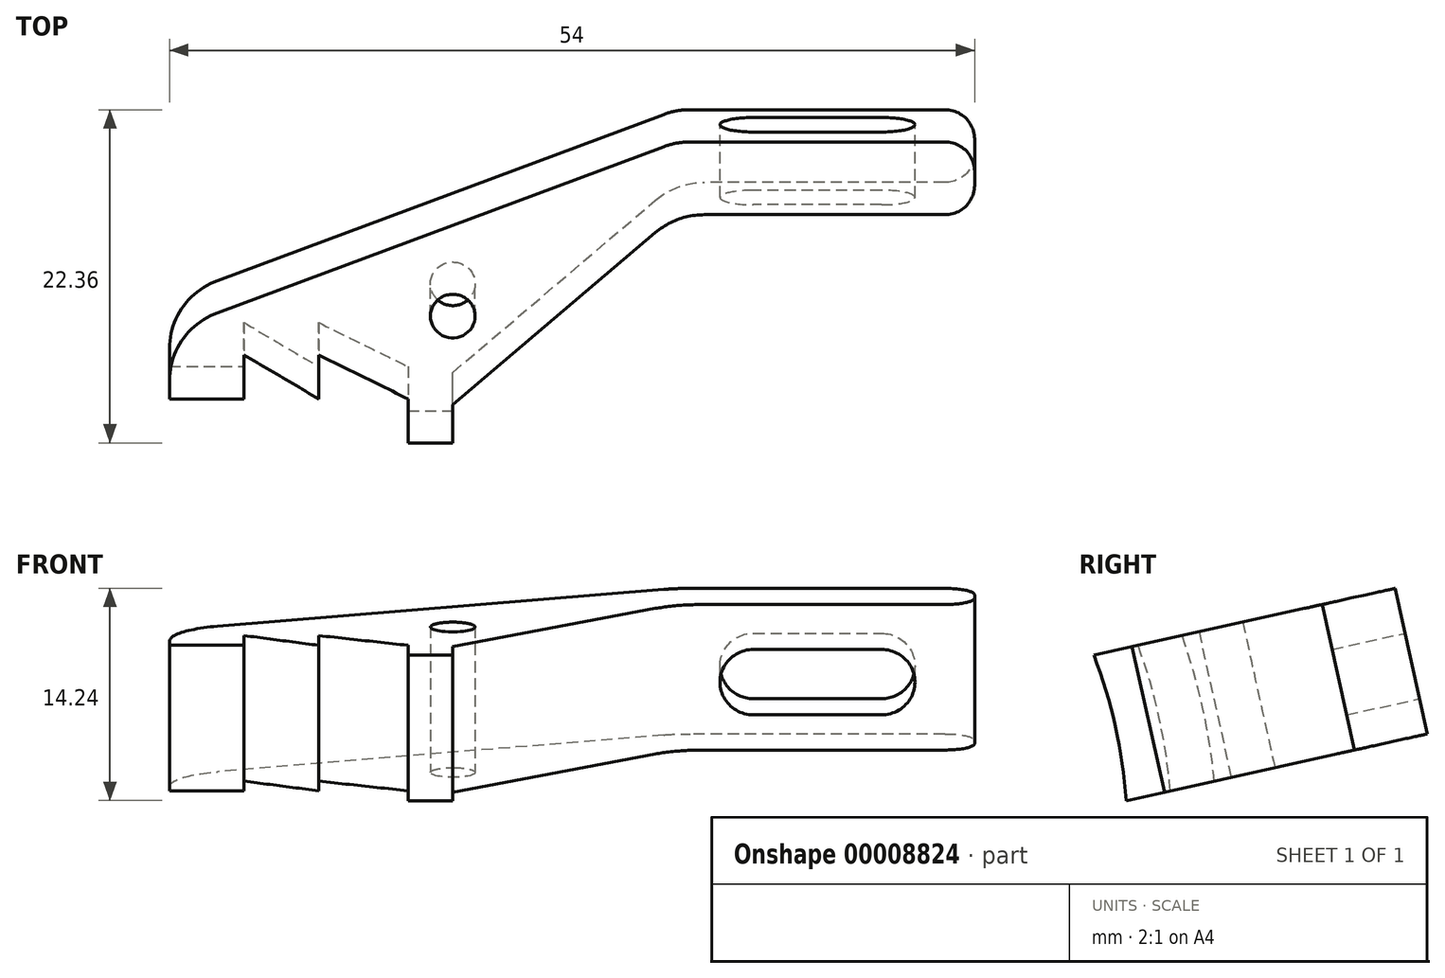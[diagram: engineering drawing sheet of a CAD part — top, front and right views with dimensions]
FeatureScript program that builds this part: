
annotation { "Feature Type Name" : "Feature", "Feature Type Description" : "" }
export const myFeature = defineFeature(function(context is Context, id is Id, definition is map)
    precondition{}
    {
        {
            var Q0;
            Q0=qCreatedBy(makeId("Top.planeOp"),FACE);
            var sketch = newSketch(context, id + "F0", { "sketchPlane" : qUnion([Q0])});
            skLineSegment(sketch, "E0", {"start": v(0, 0) * mm, "end": v(5, 0) * mm});
            skLineSegment(sketch, "E1", {"start": v(5, 0) * mm, "end": v(5, 3) * mm});
            skLineSegment(sketch, "E2", {"start": v(5, 3) * mm, "end": v(10, 0) * mm});
            skLineSegment(sketch, "E3", {"start": v(10, 0) * mm, "end": v(10, 3) * mm});
            skLineSegment(sketch, "E4", {"start": v(10, 3) * mm, "end": v(16, 0) * mm});
            skLineSegment(sketch, "E5", {"start": v(16, 0) * mm, "end": v(16, -3) * mm});
            skLineSegment(sketch, "E6", {"start": v(16, -3) * mm, "end": v(19, -3) * mm});
            skLineSegment(sketch, "E7", {"start": v(19, -3) * mm, "end": v(19, 5) * mm});
            skLineSegment(sketch, "E8", {"start": v(19, 5) * mm, "end": v(0, 5) * mm});
            skLineSegment(sketch, "E9", {"start": v(0, 5) * mm, "end": v(0, 0) * mm});
            skSolve(sketch);
        }
        {
            var Q0;
            Q0=qCreatedBy(makeId("Right.planeOp"),FACE);
            var sketch = newSketch(context, id + "F1", { "sketchPlane" : qUnion([Q0])});
            skArc(sketch, "E10", {"start": v(3, 0) * mm, "mid": v(2.05, 8.66) * mm, "end": v(-0.75, 16.9) * mm});
            skLineSegment(sketch, "E11", {"start": v(3, 0) * mm, "end": v(-37, 0) * mm});
            skLineSegment(sketch, "E12", {"start": v(-37, 0) * mm, "end": v(-0.75, 16.9) * mm});
            skSolve(sketch);
        }
        {
            var Q0;
            Q0=makeQuery(id+"F0.imprint","IMPRINT",FACE,{"disambiguationData":[TD([[makeQuery(id+"F0.imprint","IMPRINT",EDGE,{"derivedFrom":sQuery(id+"F0.wireOp",EDGE,"E0")}),1.0]])]});
            var Q1;
            Q1=sQuery(id+"F1.wireOp",EDGE,"E10");
            sweep(context, id + "F2", {"profiles" : qUnion([Q0]), "path" : qUnion([Q1])});
        }
        {
            var Q0;
            Q0=makeQuery(id+"F2.opSweep","SWEPT_FACE",FACE,{"disambiguationData":[OSD([sQuery(id+"F0.wireOp",EDGE,"E7"),sQuery(id+"F1.wireOp",EDGE,"E10")])]});
            var sketch = newSketch(context, id + "F3", { "sketchPlane" : qUnion([Q0])});
            skLineSegment(sketch, "E13.rect.bottom", {"start": v(4.96, 1.77) * mm, "end": v(-3, 0) * mm});
            skLineSegment(sketch, "E13.rect.top", {"start": v(1.78, 16.13) * mm, "end": v(-6.19, 14.37) * mm});
            skLineSegment(sketch, "E13.rect.left", {"start": v(4.96, 1.77) * mm, "end": v(1.78, 16.13) * mm});
            skLineSegment(sketch, "E13.rect.right", {"start": v(-3, 0) * mm, "end": v(-6.19, 14.37) * mm});
            skPoint(sketch, "E13.rect.middle", {"position": v(-0.61, 8.07) * mm});
            skSolve(sketch);
        }
        {
            var Q0;
            Q0=makeQuery(id+"F3.imprint","IMPRINT",FACE,{"disambiguationData":[TD([[makeQuery(id+"F3.imprint","IMPRINT",EDGE,{"derivedFrom":sQuery(id+"F3.wireOp",EDGE,"E13.rect.bottom")}),-1.0]])]});
            extrude(context, id + "F4", {"entities" : qUnion([Q0]), "operationType" : NewBodyOperationType.INTERSECT, "endBound" : BoundingType.THROUGH_ALL, "oppositeDirection" : true, "depth" : 25 * mm});
        }
        {
            var Q0;
            Q0=makeQuery(id+"F4.boolean.opBoolean","COPY",FACE,{"derivedFrom":makeQuery(id+"F4.opExtrude","SWEPT_FACE",FACE,{"disambiguationData":[OSD([sQuery(id+"F3.wireOp",EDGE,"E13.rect.bottom")])]})});
            var sketch = newSketch(context, id + "F5", { "sketchPlane" : qUnion([Q0])});
            skLineSegment(sketch, "E14", {"start": v(34, -13.2) * mm, "end": v(54, -13.2) * mm});
            skLineSegment(sketch, "E15", {"start": v(54, -13.2) * mm, "end": v(54, -18.2) * mm});
            skLineSegment(sketch, "E16", {"start": v(54, -18.2) * mm, "end": v(34, -18.2) * mm});
            skLineSegment(sketch, "E17", {"start": v(34, -13.2) * mm, "end": v(19, -0.14) * mm});
            skCircle(sketch, "E18", {"center": v(19, -6.23) * mm, "radius": 1.5 * mm});
            skLineSegment(sketch, "E19", {"start": v(0, -5.23) * mm, "end": v(34, -18.2) * mm});
            skSolve(sketch);
        }
        {
            var Q0;
            Q0=makeQuery(id+"F5.imprint","IMPRINT",FACE,{"disambiguationData":[TD([[makeQuery(id+"F5.imprint","IMPRINT",EDGE,{"derivedFrom":sQuery(id+"F5.wireOp",EDGE,"E14")}),-1.0]])]});
            var Q1;
            {var subQ0=sQuery(id+"F3.wireOp",EDGE,"E13.rect.bottom");var subQ1=makeQuery(id+"F4.boolean.opBoolean","COPY",EDGE,{"derivedFrom":makeQuery(id+"F4.opExtrude","CAP_EDGE",EDGE,{"disambiguationData":[OSD([subQ0])],"isStart":true})});var subQ2=sQuery(id+"F5.wireOp",EDGE,"E18");var subQ3=makeQuery(id+"F5.imprint","INTERSECT",VERTEX,{"derivedFrom":[subQ1,subQ2]});Q1=makeQuery(id+"F5.imprint","IMPRINT",FACE,{"disambiguationData":[TD([[makeQuery(id+"F5.imprint","IMPRINT",EDGE,{"disambiguationData":[TD([[subQ3,-1.0]])],"derivedFrom":subQ2}),1.0]])]});}
            var Q2;
            Q2=makeQuery(id+"F4.boolean.opBoolean","COPY",FACE,{"derivedFrom":makeQuery(id+"F4.opExtrude","SWEPT_FACE",FACE,{"disambiguationData":[OSD([sQuery(id+"F3.wireOp",EDGE,"E13.rect.top")])]})});
            extrude(context, id + "F6", {"entities" : qUnion([Q0, Q1]), "operationType" : NewBodyOperationType.ADD, "endBound" : BoundingType.UP_TO_SURFACE, "oppositeDirection" : true, "endBoundEntityFace" : qUnion([Q2]), "depth" : 25 * mm});
        }
        {
            var Q0;
            {var subQ0=sQuery(id+"F3.wireOp",EDGE,"E13.rect.bottom");var subQ1=makeQuery(id+"F4.boolean.opBoolean","COPY",EDGE,{"derivedFrom":makeQuery(id+"F4.opExtrude","CAP_EDGE",EDGE,{"disambiguationData":[OSD([subQ0])],"isStart":true})});var subQ2=sQuery(id+"F5.wireOp",EDGE,"E18");var subQ3=makeQuery(id+"F5.imprint","INTERSECT",VERTEX,{"derivedFrom":[subQ1,subQ2]});Q0=makeQuery(id+"F5.imprint","IMPRINT",FACE,{"disambiguationData":[TD([[makeQuery(id+"F5.imprint","IMPRINT",EDGE,{"disambiguationData":[TD([[subQ3,-1.0]])],"derivedFrom":subQ2}),1.0]])]});}
            var Q1;
            {var subQ0=sQuery(id+"F3.wireOp",EDGE,"E13.rect.top");Q1=makeQuery(id+"F6.boolean.opBoolean","MERGE",FACE,{"derivedFrom":[makeQuery(id+"F4.boolean.opBoolean","COPY",FACE,{"derivedFrom":makeQuery(id+"F4.opExtrude","SWEPT_FACE",FACE,{"disambiguationData":[OSD([subQ0])]})}),makeQuery(id+"F6.opExtrude","CAP_FACE",FACE,{"disambiguationData":[OSD([subQ0]),ownerDisambiguation([makeQuery(id+"F6.opExtrude","SWEPT_BODY",BODY,{"disambiguationData":[OSD([sQuery(id+"F0.wireOp",EDGE,"E7"),sQuery(id+"F0.wireOp",EDGE,"E8"),sQuery(id+"F1.wireOp",EDGE,"E10"),sQuery(id+"F3.wireOp",EDGE,"E13.rect.bottom"),sQuery(id+"F3.wireOp",EDGE,"E13.rect.left"),sQuery(id+"F5.wireOp",EDGE,"E14"),sQuery(id+"F5.wireOp",EDGE,"E15"),sQuery(id+"F5.wireOp",EDGE,"E16"),sQuery(id+"F5.wireOp",EDGE,"E17"),sQuery(id+"F5.wireOp",EDGE,"E18"),sQuery(id+"F5.wireOp",EDGE,"E19")])]})])],"isStart":false})]});}
            extrude(context, id + "F7", {"entities" : qUnion([Q0]), "operationType" : NewBodyOperationType.REMOVE, "endBound" : BoundingType.UP_TO_SURFACE, "oppositeDirection" : true, "endBoundEntityFace" : qUnion([Q1]), "depth" : 25 * mm});
        }
        {
            var Q0;
            Q0=makeQuery(id+"F6.opExtrude","SWEPT_EDGE",EDGE,{"disambiguationData":[OSD([sQuery(id+"F5.wireOp",EDGE,"E16"),sQuery(id+"F5.wireOp",EDGE,"E19")])]});
            var Q1;
            {var subQ0=sQuery(id+"F3.wireOp",EDGE,"E13.rect.left");var subQ1=sQuery(id+"F1.wireOp",EDGE,"E10");var subQ2=sQuery(id+"F0.wireOp",EDGE,"E9");Q1=makeQuery(id+"F6.boolean.opBoolean","MERGE",EDGE,{"derivedFrom":[makeQuery(id+"F4.boolean.opBoolean","INTERSECT",EDGE,{"derivedFrom":[makeQuery(id+"F2.opSweep","SWEPT_FACE",FACE,{"disambiguationData":[OSD([subQ2,subQ1])]}),makeQuery(id+"F4.opExtrude","SWEPT_FACE",FACE,{"disambiguationData":[OSD([subQ0])]})]}),makeQuery(id+"F6.opExtrude","SWEPT_EDGE",EDGE,{"disambiguationData":[OSD([sQuery(id+"F0.wireOp",EDGE,"E7"),sQuery(id+"F0.wireOp",EDGE,"E8"),subQ2,subQ1,sQuery(id+"F3.wireOp",EDGE,"E13.rect.bottom"),subQ0,sQuery(id+"F5.wireOp",EDGE,"E19")])]})]});}
            var Q2;
            Q2=makeQuery(id+"F6.opExtrude","SWEPT_EDGE",EDGE,{"disambiguationData":[OSD([sQuery(id+"F5.wireOp",EDGE,"E14"),sQuery(id+"F5.wireOp",EDGE,"E17")])]});
            var Q3;
            Q3=makeQuery(id+"F6.opExtrude","SWEPT_EDGE",EDGE,{"disambiguationData":[OSD([sQuery(id+"F3.wireOp",EDGE,"E13.rect.bottom"),sQuery(id+"F5.wireOp",EDGE,"E17")])]});
            fillet(context, id + "F8", {"entities" : qUnion([Q0, Q1, Q2, Q3]), "radius" : 5 * mm, "tangentPropagation" : true, "allowEdgeOverflow" : false});
        }
        {
            var Q0;
            Q0=makeQuery(id+"F6.opExtrude","SWEPT_EDGE",EDGE,{"disambiguationData":[OSD([sQuery(id+"F5.wireOp",EDGE,"E15"),sQuery(id+"F5.wireOp",EDGE,"E16")])]});
            var Q1;
            Q1=makeQuery(id+"F6.opExtrude","SWEPT_EDGE",EDGE,{"disambiguationData":[OSD([sQuery(id+"F5.wireOp",EDGE,"E14"),sQuery(id+"F5.wireOp",EDGE,"E15")])]});
            fillet(context, id + "F9", {"entities" : qUnion([Q0, Q1]), "radius" : 2 * mm, "tangentPropagation" : true, "allowEdgeOverflow" : false});
        }
        {
            var Q0;
            Q0=makeQuery(id+"F6.opExtrude","SWEPT_FACE",FACE,{"disambiguationData":[OSD([sQuery(id+"F5.wireOp",EDGE,"E16")])]});
            var sketch = newSketch(context, id + "F10", { "sketchPlane" : qUnion([Q0])});
            skLineSegment(sketch, "E20.rect.bottom", {"start": v(-39.17, 5.42) * mm, "end": v(-47.75, 5.42) * mm});
            skLineSegment(sketch, "E20.rect.top", {"start": v(-39.17, 9.92) * mm, "end": v(-47.75, 9.92) * mm});
            skLineSegment(sketch, "E20.rect.left", {"start": v(-39.17, 5.42) * mm, "end": v(-39.17, 9.92) * mm, "construction": true});
            skLineSegment(sketch, "E20.rect.right", {"start": v(-47.75, 5.42) * mm, "end": v(-47.75, 9.92) * mm, "construction": true});
            skPoint(sketch, "E20.rect.middle", {"position": v(-43.46, 7.67) * mm});
            skArc(sketch, "E21", {"start": v(-47.75, 9.92) * mm, "mid": v(-50, 7.67) * mm, "end": v(-47.75, 5.42) * mm});
            skArc(sketch, "E22", {"start": v(-39.17, 5.42) * mm, "mid": v(-36.92, 7.67) * mm, "end": v(-39.17, 9.92) * mm});
            skPoint(sketch, "E23", {"position": v(-43.46, 15.37) * mm});
            skSolve(sketch);
        }
        {
            var Q0;
            Q0=makeQuery(id+"F10.imprint","IMPRINT",FACE,{"disambiguationData":[TD([[makeQuery(id+"F10.imprint","IMPRINT",EDGE,{"derivedFrom":sQuery(id+"F10.wireOp",EDGE,"E20.rect.bottom")}),-1.0]])]});
            var Q1;
            Q1=makeQuery(id+"F6.opExtrude","SWEPT_FACE",FACE,{"disambiguationData":[OSD([sQuery(id+"F5.wireOp",EDGE,"E14")])]});
            extrude(context, id + "F11", {"entities" : qUnion([Q0]), "operationType" : NewBodyOperationType.REMOVE, "endBound" : BoundingType.UP_TO_SURFACE, "oppositeDirection" : true, "endBoundEntityFace" : qUnion([Q1]), "depth" : 25 * mm});
        }
        {
            var Q0;
            Q0=qCreatedBy(makeId("Right.planeOp"),FACE);
            var sketch = newSketch(context, id + "F12", { "sketchPlane" : qUnion([Q0])});
            skLineSegment(sketch, "E24.bottom", {"start": v(17.11, 6.87) * mm, "end": v(-3.51, 2.3) * mm});
            skLineSegment(sketch, "E24.top", {"start": v(14.95, 16.64) * mm, "end": v(-5.67, 12.07) * mm});
            skLineSegment(sketch, "E24.left", {"start": v(17.11, 6.87) * mm, "end": v(14.95, 16.64) * mm});
            skLineSegment(sketch, "E24.right", {"start": v(-3.51, 2.3) * mm, "end": v(-5.67, 12.07) * mm});
            skLineSegment(sketch, "E25.0", {"start": v(17.62, 4.57) * mm, "end": v(14.44, 18.94) * mm});
            skArc(sketch, "E26.0", {"start": v(-3, 0) * mm, "mid": v(-3.8, 7.36) * mm, "end": v(-6.19, 14.37) * mm, "construction": true});
            skLineSegment(sketch, "E27", {"start": v(-3, 0) * mm, "end": v(-6.19, 14.37) * mm, "construction": true});
            skPoint(sketch, "E28", {"position": v(-4.6, 7.18) * mm});
            skSolve(sketch);
        }
        {
            var Q0;
            {var subQ2=sQuery(id+"F12.wireOp",EDGE,"E24.bottom");Q0=makeQuery(id+"F12.imprint","IMPRINT",FACE,{"disambiguationData":[TD([[makeQuery(id+"F12.imprint","IMPRINT",EDGE,{"derivedFrom":subQ2}),-1.0]])]});}
            extrude(context, id + "F13", {"entities" : qUnion([Q0]), "operationType" : NewBodyOperationType.INTERSECT, "endBound" : BoundingType.THROUGH_ALL, "depth" : 25 * mm});
        }
    });
